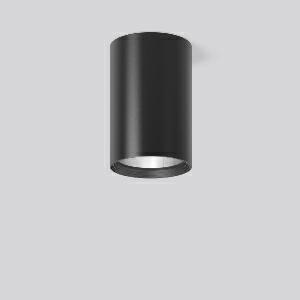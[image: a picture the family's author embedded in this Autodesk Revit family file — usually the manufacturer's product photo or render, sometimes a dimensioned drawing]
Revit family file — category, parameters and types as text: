
# Revit family: heledon_maxi_a_931218_003_2_e868
name_source: partatom
category: Lighting Fixtures
units: mm (PartAtom-declared; Revit-internal decimal feet)

## family parameters
Cut with Voids When Loaded = No
Host = Face
Light Source = No
Part Type = Normal
Room Calculation Point = No
Round Connector Dimension = Use Diameter
Shared = No

## types (1)
- HELEDON maxi A (1 x LED Modul 927, 3150 lm, 2700)
    Apparent Load = 25 VA
    Approval mark = CE
    CIE Flux Codes = 100 100 100 100 100
    Color Rendering = 92
    Color Temperature = 2700
    Default Elevation = 1800 mm
    Description = Series: HELEDON maxi
Cylindrical surface-mounted downlight. Housing: die-cast aluminium, powder-coated. Internal ceiling frame polycarbonate with bayonet mounting. Black plastic ring and recessed LED to prevent glare from the side. Optical assembly with reflector made of MIRO-Silver with 98% total light reflection for outstanding efficiency - can be changed without tools. Best colour rendering index Ra>90. Suitable for Ceiling mounting. Easy installation with a separate ceiling frame with bayonet mounting and plug connection. Driver integrated. Connected via plug-in connector. High quality converter without flickering and stroboscopic effect. The following accessories can be mounted without use of tools: interchangeable lenses, decorative glasses, honeycomb louvre, clear and frosted diffusers, white interchangeable plastic ring. 
Colour: deep black, matt (RAL 9005)
Diameter: 123 mm
Height: 183 mm
Lamp: LED
Socket: without socket
Colour temperature: 2700K
Colour rendering index (CRI): 92
System power: 25 W
Rated luminous flux: 3150 lm
Luminous efficiency: 126 lm/W
Control gear: Regulated power supply
Protection class: I
Type of protection: IP 20
    Height = 183 mm
    Lamp = 1 x LED Modul 927
    Lamp Light Flux = 3150 lm
    Lamp count = 1
    Length = 123 mm
    Lifetime = 50000 h
    Luminous efficacy = 126 lm/W
    Manufacturer = RZB
    ModVariant = No
    Model = 931218.003.2
    Mounting Place = Ceiling
    Mounting Type = Surface mounted
    Number of Poles = 1
    OnlyDefault = Yes
    Power Factor = 1
    Product Name = HELEDON maxi A
    Product group = Surface mounted downlights
    ProductGroupID = 302
    Protection Class = Protection class I
    Protection Degree = IP 20
    RLX_Detail_Level = 1
    RLX_Emergency_Light_Flux = 0 lm
    RLX_Emergency_Type = 0
    RLX_Emergency_Type_DB = No
    RlxData = <blob elided: 97501 chars, md5=60464b19>
    Socket = socket
    Standby Power = 0 W
    System Light Flux = 3150 lm
    System Power = 25 W
    Type Comments = Product without accessories
    Type Image = 931192.003.jpg
    URL = http://relux.com
    VarID = ---
    Voltage = 230 V
    Voltage Range = 220-240 V
    Weight = 0.00 kg
    Width = 0 mm  [stored 0 ft]

note: [stored X ft] marks values corroborated as IEEE doubles in the binary element streams (Revit-internal decimal feet)

## geometry (parser evidence)
native form markers: Blend x4, Sweep x12
no freeform markers — native parametric forms only
